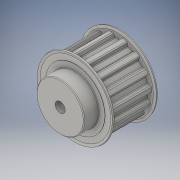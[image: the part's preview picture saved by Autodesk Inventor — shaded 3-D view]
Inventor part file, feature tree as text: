
AUTODESK INVENTOR PART (.ipt)
format: ipt  version: 2016 (Build 200138000, 138)  size: 370,688 bytes
history: native  units: in
note: dims shown in document units (in); Inventor stores cm internally (conversion verified against a paired STEP export)
features: other x3, sketch x1
ambient origin geometry x8: Origin, YZ Plane, XZ Plane, XY Plane, X Axis, Y Axis, Z Axis, Center Point
bodies: Solid1 (feature_tree)
feature tree (4):
  other  "ls40t10_15-2_hub-32x10_d-8h7.ipt"
  other  "Solid1::ls40t10_15-2_hub-32x10_d-8h7.ipt"
  other  "TaggingFeature1"
  sketch  "Sketch1"  dims[d0=0.3937in]
